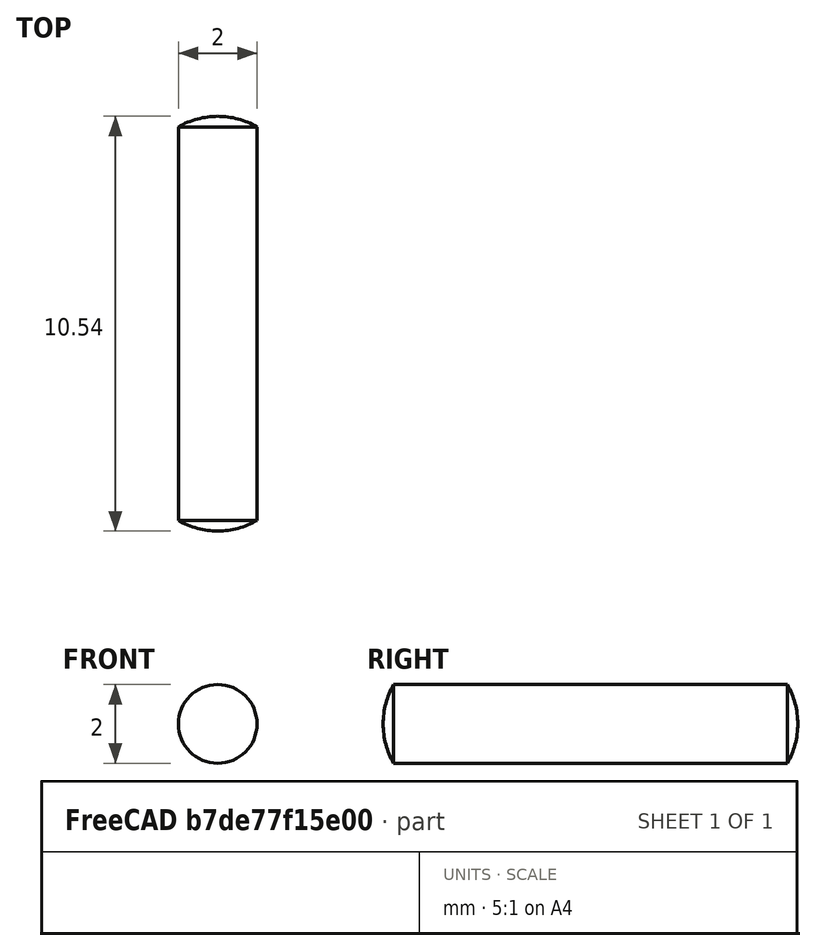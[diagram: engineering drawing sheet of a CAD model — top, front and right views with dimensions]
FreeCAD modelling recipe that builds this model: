
FCSTD DOCUMENT  (FreeCAD 0.15R4470 (Git))
Label: Zyl-Stift_DIN_7-2x10
License: CC-BY 3.0
LicenseURL: http://creativecommons.org/licenses/by/3.0/
objects: Sketcher::SketchObject×1, PartDesign::Revolution×1
note: 3 computed .brp shape members not serialized (recipe doc carries the construction recipe); baked Part::Feature solids carry a one-line shape summary decoded from their .brp

FEATURE [Sketcher::SketchObject] Sketch
  Placement = pos=(0,0,0) rot=(0.57735,0.57735,0.57735;2.0944rad)
  sketch-geometry (4):
    g0: ArcOfCircle CenterX=8.26795 CenterY=0 CenterZ=0 NormalX=0 NormalY=0 NormalZ=1 Radius=2 StartAngle=0 EndAngle=0.523599
    g1: LineSegment StartX=0 StartY=1 StartZ=0 EndX=10 EndY=1 EndZ=0
    g2: LineSegment StartX=-0.267949 StartY=0 StartZ=0 EndX=10.2679 EndY=0 EndZ=0
    g3: ArcOfCircle CenterX=1.73205 CenterY=0 CenterZ=0 NormalX=0 NormalY=0 NormalZ=1 Radius=2 StartAngle=2.61799 EndAngle=3.14159
  constraints (14):
    c: PointOnObject(g2,g-1)
    c: PointOnObject(g1,g-2)
    c: Coincident(g0,g1)
    c: PointOnObject(g0,g-1)
    c: Horizontal(g1)
    c: Coincident(g2,g0)
    c: Horizontal(g2)
    c: Radius(g0) = 2
    c: PointOnObject(g3,g2)
    c: Coincident(g3,g1)
    c: Coincident(g3,g2)
    c: Equal(g3,g0)
    c: DistanceY(g-1,g1) = 1
    c: DistanceX(g1) = 10
FEATURE [PartDesign::Revolution] Revolution  label="Zyl-Stift DIN 7-2x10 #"
  Angle = 360
  Axis = (0,1,0)
  Base = (0,0,0)
  Placement = pos=(0,0,0) rot=(0.57735,0.57735,0.57735;2.0944rad)
  ReferenceAxis = -> Sketch [H_Axis]
  Sketch = -> Sketch
